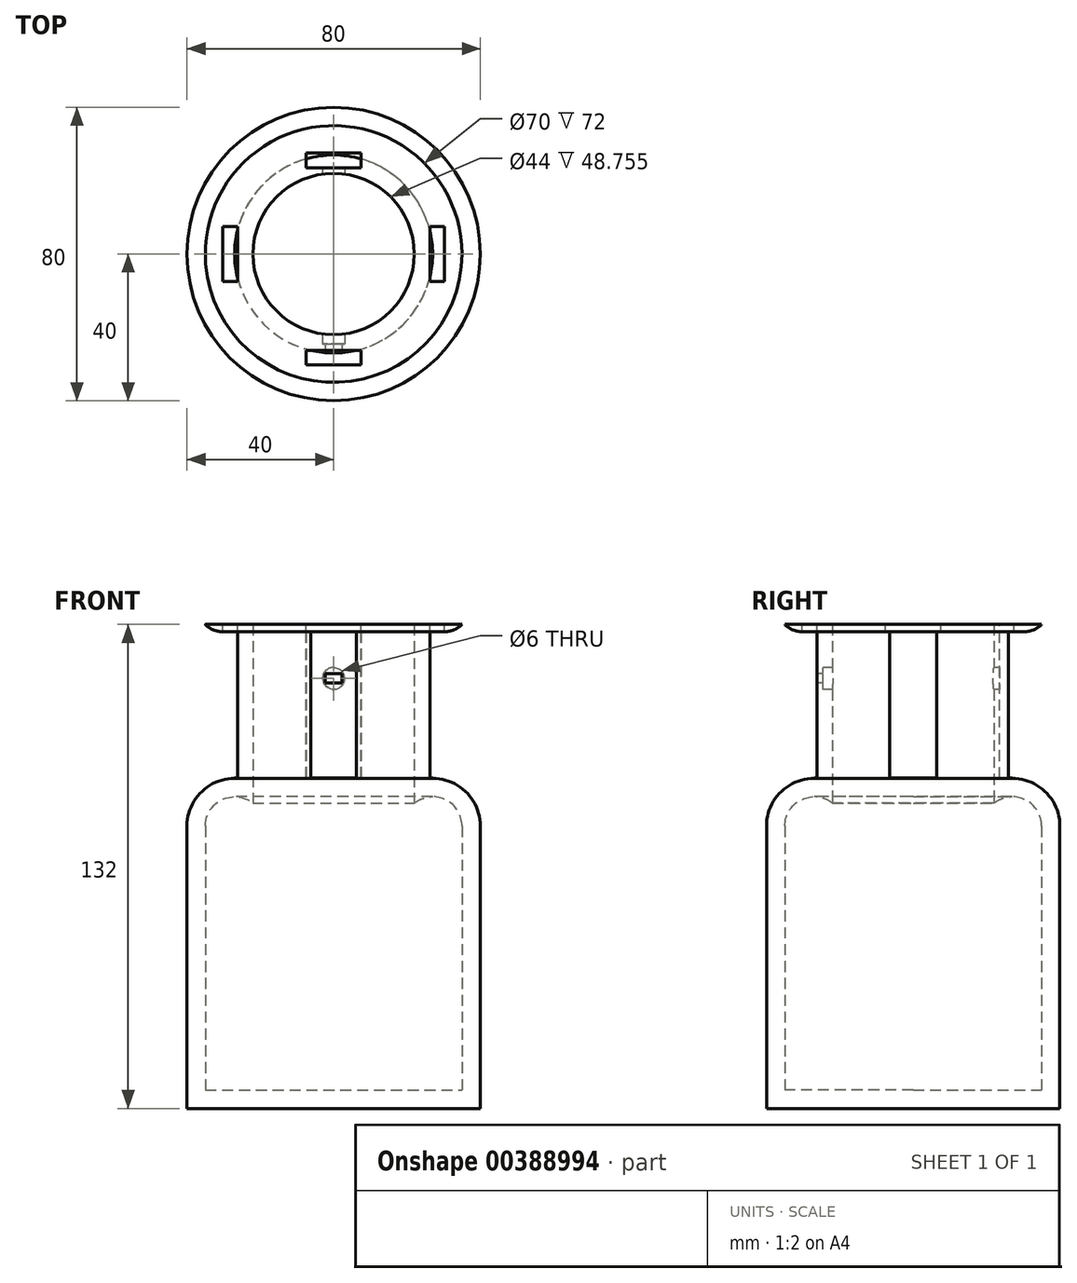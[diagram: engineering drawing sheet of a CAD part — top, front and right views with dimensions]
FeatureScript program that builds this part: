
annotation { "Feature Type Name" : "Feature", "Feature Type Description" : "" }
export const myFeature = defineFeature(function(context is Context, id is Id, definition is map)
    precondition{}
    {
        {
            var Q0;
            Q0=qCreatedBy(makeId("Top.planeOp"),FACE);
            var sketch = newSketch(context, id + "F0", { "sketchPlane" : qUnion([Q0])});
            skCircle(sketch, "E0", {"center": v(0, 0) * mm, "radius": 40 * mm});
            skSolve(sketch);
        }
        {
            var Q0;
            Q0=makeQuery(id+"F0.imprint","IMPRINT",FACE,{"disambiguationData":[TD([[makeQuery(id+"F0.imprint","IMPRINT",EDGE,{"derivedFrom":sQuery(id+"F0.wireOp",EDGE,"E0")}),1.0]])]});
            extrude(context, id + "F1", {"entities" : qUnion([Q0]), "depth" : 90 * mm});
        }
        {
            var Q0;
            Q0=makeQuery(id+"F1.opExtrude","CAP_FACE",FACE,{"disambiguationData":[OSD([sQuery(id+"F0.wireOp",EDGE,"E0")])],"isStart":false});
            fillet(context, id + "F2", {"entities" : qUnion([Q0]), "radius" : 13 * mm, "tangentPropagation" : true, "allowEdgeOverflow" : false});
        }
        {
            var Q0;
            Q0=makeQuery(id+"F1.opExtrude","CAP_FACE",FACE,{"disambiguationData":[OSD([sQuery(id+"F0.wireOp",EDGE,"E0")])],"isStart":false});
            extrude(context, id + "F3", {"entities" : qUnion([Q0]), "operationType" : NewBodyOperationType.ADD, "depth" : 40 * mm});
        }
        {
            var Q0;
            Q0=makeQuery(id+"F3.opExtrude","CAP_FACE",FACE,{"disambiguationData":[OSD([sQuery(id+"F0.wireOp",EDGE,"E0")])],"isStart":false});
            shell(context, id + "F4", {"entities" : qUnion([Q0]), "thickness" : 5 * mm});
        }
        {
            var Q0;
            Q0=makeQuery(id+"F3.opExtrude","CAP_FACE",FACE,{"disambiguationData":[OSD([sQuery(id+"F0.wireOp",EDGE,"E0")])],"isStart":false});
            var sketch = newSketch(context, id + "F5", { "sketchPlane" : qUnion([Q0])});
            skCircle(sketch, "E1.0.0", {"center": v(0, 0) * mm, "radius": 27 * mm});
            skCircle(sketch, "E2", {"center": v(0, 0) * mm, "radius": 35 * mm});
            skSolve(sketch);
        }
        {
            var Q0;
            Q0=makeQuery(id+"F5.imprint","IMPRINT",FACE,{"disambiguationData":[TD([[makeQuery(id+"F5.imprint","IMPRINT",EDGE,{"derivedFrom":sQuery(id+"F5.wireOp",EDGE,"E1.0.0")}),-1.0]])]});
            var Q1;
            Q1=makeQuery(id+"F5.imprint","IMPRINT",FACE,{"disambiguationData":[TD([[makeQuery(id+"F5.imprint","IMPRINT",EDGE,{"derivedFrom":sQuery(id+"F5.wireOp",EDGE,"E1.0.0")}),1.0]])]});
            extrude(context, id + "F6", {"entities" : qUnion([Q0, Q1]), "operationType" : NewBodyOperationType.ADD, "depth" : 2 * mm});
        }
        {
            var Q0;
            Q0=makeQuery(id+"F6.opExtrude","CAP_EDGE",EDGE,{"disambiguationData":[OSD([sQuery(id+"F5.wireOp",EDGE,"E2")])],"isStart":true});
            fillet(context, id + "F7", {"entities" : qUnion([Q0]), "radius" : 6.5 * mm, "tangentPropagation" : true, "allowEdgeOverflow" : false});
        }
        {
            var Q0;
            Q0=makeQuery(id+"F6.opExtrude","CAP_FACE",FACE,{"disambiguationData":[OSD([sQuery(id+"F0.wireOp",EDGE,"E0"),sQuery(id+"F5.wireOp",EDGE,"E2")])],"isStart":false});
            var sketch = newSketch(context, id + "F8", { "sketchPlane" : qUnion([Q0])});
            skCircle(sketch, "E3.0.0", {"center": v(0, 0) * mm, "radius": 35 * mm});
            skCircle(sketch, "E4.0", {"center": v(0, 0) * mm, "radius": 22 * mm});
            skLineSegment(sketch, "E5.bottom", {"start": v(7.5, 23.5) * mm, "end": v(-7.5, 23.5) * mm});
            skLineSegment(sketch, "E5.top", {"start": v(7.5, 27.5) * mm, "end": v(-7.5, 27.5) * mm});
            skLineSegment(sketch, "E5.left", {"start": v(7.5, 23.5) * mm, "end": v(7.5, 27.5) * mm});
            skLineSegment(sketch, "E5.right", {"start": v(-7.5, 23.5) * mm, "end": v(-7.5, 27.5) * mm});
            skPoint(sketch, "E5.middle", {"position": v(0, 25.5) * mm});
            skLineSegment(sketch, "E6.bottom", {"start": v(-26.22, -7.5) * mm, "end": v(-30.22, -7.5) * mm});
            skLineSegment(sketch, "E6.top", {"start": v(-26.22, 7.5) * mm, "end": v(-30.22, 7.5) * mm});
            skLineSegment(sketch, "E6.left", {"start": v(-26.22, -7.5) * mm, "end": v(-26.22, 7.5) * mm});
            skLineSegment(sketch, "E6.right", {"start": v(-30.22, -7.5) * mm, "end": v(-30.22, 7.5) * mm});
            skPoint(sketch, "E6.middle", {"position": v(-28.22, 0) * mm});
            skLineSegment(sketch, "E7.bottom", {"start": v(7.5, -30.26) * mm, "end": v(-7.5, -30.26) * mm});
            skLineSegment(sketch, "E7.top", {"start": v(7.5, -26.26) * mm, "end": v(-7.5, -26.26) * mm});
            skLineSegment(sketch, "E7.left", {"start": v(7.5, -30.26) * mm, "end": v(7.5, -26.26) * mm});
            skLineSegment(sketch, "E7.right", {"start": v(-7.5, -30.26) * mm, "end": v(-7.5, -26.26) * mm});
            skPoint(sketch, "E7.middle", {"position": v(0, -28.26) * mm});
            skLineSegment(sketch, "E8.bottom", {"start": v(30.22, -7.5) * mm, "end": v(26.22, -7.5) * mm});
            skLineSegment(sketch, "E8.top", {"start": v(30.22, 7.5) * mm, "end": v(26.22, 7.5) * mm});
            skLineSegment(sketch, "E8.left", {"start": v(30.22, -7.5) * mm, "end": v(30.22, 7.5) * mm});
            skLineSegment(sketch, "E8.right", {"start": v(26.22, -7.5) * mm, "end": v(26.22, 7.5) * mm});
            skPoint(sketch, "E8.middle", {"position": v(28.22, 0) * mm});
            skLineSegment(sketch, "E9", {"start": v(0, 23.5) * mm, "end": v(0, 22) * mm, "construction": true});
            skLineSegment(sketch, "E10", {"start": v(-26.22, 0) * mm, "end": v(-22, 0) * mm, "construction": true});
            skLineSegment(sketch, "E11", {"start": v(0, -26.26) * mm, "end": v(0, -22) * mm, "construction": true});
            skLineSegment(sketch, "E12", {"start": v(26.22, 0) * mm, "end": v(22, 0) * mm, "construction": true});
            skSolve(sketch);
        }
        {
            var Q0;
            Q0=makeQuery(id+"F8.imprint","IMPRINT",FACE,{"disambiguationData":[TD([[makeQuery(id+"F8.imprint","IMPRINT",EDGE,{"derivedFrom":sQuery(id+"F8.wireOp",EDGE,"E6.bottom")}),-1.0]])]});
            var Q1;
            Q1=makeQuery(id+"F8.imprint","IMPRINT",FACE,{"disambiguationData":[TD([[makeQuery(id+"F8.imprint","IMPRINT",EDGE,{"derivedFrom":sQuery(id+"F8.wireOp",EDGE,"E5.bottom")}),-1.0]])]});
            var Q2;
            Q2=makeQuery(id+"F8.imprint","IMPRINT",FACE,{"disambiguationData":[TD([[makeQuery(id+"F8.imprint","IMPRINT",EDGE,{"derivedFrom":sQuery(id+"F8.wireOp",EDGE,"E8.bottom")}),-1.0]])]});
            var Q3;
            Q3=makeQuery(id+"F8.imprint","IMPRINT",FACE,{"disambiguationData":[TD([[makeQuery(id+"F8.imprint","IMPRINT",EDGE,{"derivedFrom":sQuery(id+"F8.wireOp",EDGE,"E7.bottom")}),-1.0]])]});
            extrude(context, id + "F9", {"entities" : qUnion([Q0, Q1, Q2, Q3]), "operationType" : NewBodyOperationType.REMOVE, "oppositeDirection" : true, "depth" : 41.9 * mm});
        }
        {
            var Q0;
            Q0=makeQuery(id+"F9.boolean.opBoolean","COPY",FACE,{"derivedFrom":makeQuery(id+"F9.opExtrude","SWEPT_FACE",FACE,{"disambiguationData":[OSD([sQuery(id+"F8.wireOp",EDGE,"E7.top")])]})});
            var sketch = newSketch(context, id + "F10", { "sketchPlane" : qUnion([Q0])});
            skLineSegment(sketch, "E13.0.0", {"start": v(7.5, 132) * mm, "end": v(-7.5, 132) * mm});
            skLineSegment(sketch, "E13.0.1", {"start": v(-7.5, 132) * mm, "end": v(-7.5, 90.1) * mm});
            skLineSegment(sketch, "E13.0.2", {"start": v(-7.5, 90.1) * mm, "end": v(7.5, 90.1) * mm});
            skLineSegment(sketch, "E13.0.3", {"start": v(7.5, 90.1) * mm, "end": v(7.5, 132) * mm});
            skCircle(sketch, "E14", {"center": v(0, 117.26) * mm, "radius": 3 * mm});
            skPoint(sketch, "E14.centerSnap0", {"position": v(0, 132) * mm});
            skLineSegment(sketch, "E15.bottom", {"start": v(2.25, 116.01) * mm, "end": v(-2.25, 116.01) * mm});
            skLineSegment(sketch, "E15.top", {"start": v(2.25, 118.51) * mm, "end": v(-2.25, 118.51) * mm});
            skLineSegment(sketch, "E15.left", {"start": v(2.25, 116.01) * mm, "end": v(2.25, 118.51) * mm});
            skLineSegment(sketch, "E15.right", {"start": v(-2.25, 116.01) * mm, "end": v(-2.25, 118.51) * mm});
            skSolve(sketch);
        }
        {
            var Q0;
            Q0=makeQuery(id+"F10.imprint","IMPRINT",FACE,{"disambiguationData":[TD([[makeQuery(id+"F10.imprint","IMPRINT",EDGE,{"derivedFrom":sQuery(id+"F10.wireOp",EDGE,"E14")}),1.0]])]});
            var Q1;
            Q1=makeQuery(id+"F10.imprint","IMPRINT",FACE,{"disambiguationData":[TD([[makeQuery(id+"F10.imprint","IMPRINT",EDGE,{"derivedFrom":sQuery(id+"F10.wireOp",EDGE,"E15.bottom")}),-1.0]])]});
            extrude(context, id + "F11", {"entities" : qUnion([Q0, Q1]), "operationType" : NewBodyOperationType.REMOVE, "endBound" : BoundingType.THROUGH_ALL, "oppositeDirection" : true, "depth" : 25 * mm});
        }
        {
            var Q0;
            Q0=makeQuery(id+"F10.imprint","IMPRINT",FACE,{"disambiguationData":[TD([[makeQuery(id+"F10.imprint","IMPRINT",EDGE,{"derivedFrom":sQuery(id+"F10.wireOp",EDGE,"E14")}),1.0]])]});
            extrude(context, id + "F12", {"entities" : qUnion([Q0]), "operationType" : NewBodyOperationType.ADD, "oppositeDirection" : true, "depth" : 1.7 * mm});
        }
    });
